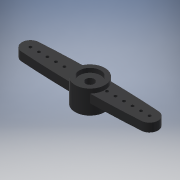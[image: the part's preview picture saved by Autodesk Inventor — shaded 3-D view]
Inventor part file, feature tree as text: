
AUTODESK INVENTOR PART (.ipt)
format: ipt  version: 2016 (Build 200138000, 138)  size: 207,360 bytes
history: native  units: mm
features: extrude x6, sketch x6, projected_geometry x4
ambient origin geometry x8: Origin, YZ Plane, XZ Plane, XY Plane, X Axis, Y Axis, Z Axis, Center Point
bodies: Solid1 (feature_tree)
feature tree (16):
  extrude  "Extrusion1"  Depth=7.0mm
  extrude  "Extrusion2"  Depth=2.0mm TaperAngle=0.0deg
  extrude  "Extrusion3"  Depth=2.0mm
  extrude  "Extrusion4"  Depth=2.0mm
  extrude  "Extrusion5"  Depth=10.0mm
  extrude  "Extrusion6"  Depth=10.0mm
  sketch  "Sketch1"  dims[d0=5.0mm d1=7.0mm]
  sketch  "Sketch2"  dims[d2=2.5mm d3=0.0mm d8=2.0mm d9=0.0mm]
  sketch  "Sketch3"  dims[d10=2.0mm d11=0.0mm d12=5.0mm]
  projected_geometry  "Projected Loop1"
  projected_geometry  "Projected Loop2"
  projected_geometry  "Projected Loop3"
  sketch  "Sketch4"  dims[d13=1.0mm d14=0.0mm d15=2.0mm]
  sketch  "Sketch5"  dims[d16=10.0mm d17=0.0mm d18=0.7mm]
  sketch  "Sketch6"  dims[d19=2.0mm d25=0.7mm d26=0.7mm d27=0.7mm d28=0.7mm d29=10.0mm d30=0.0mm]
  projected_geometry  "Projected Loop4"
